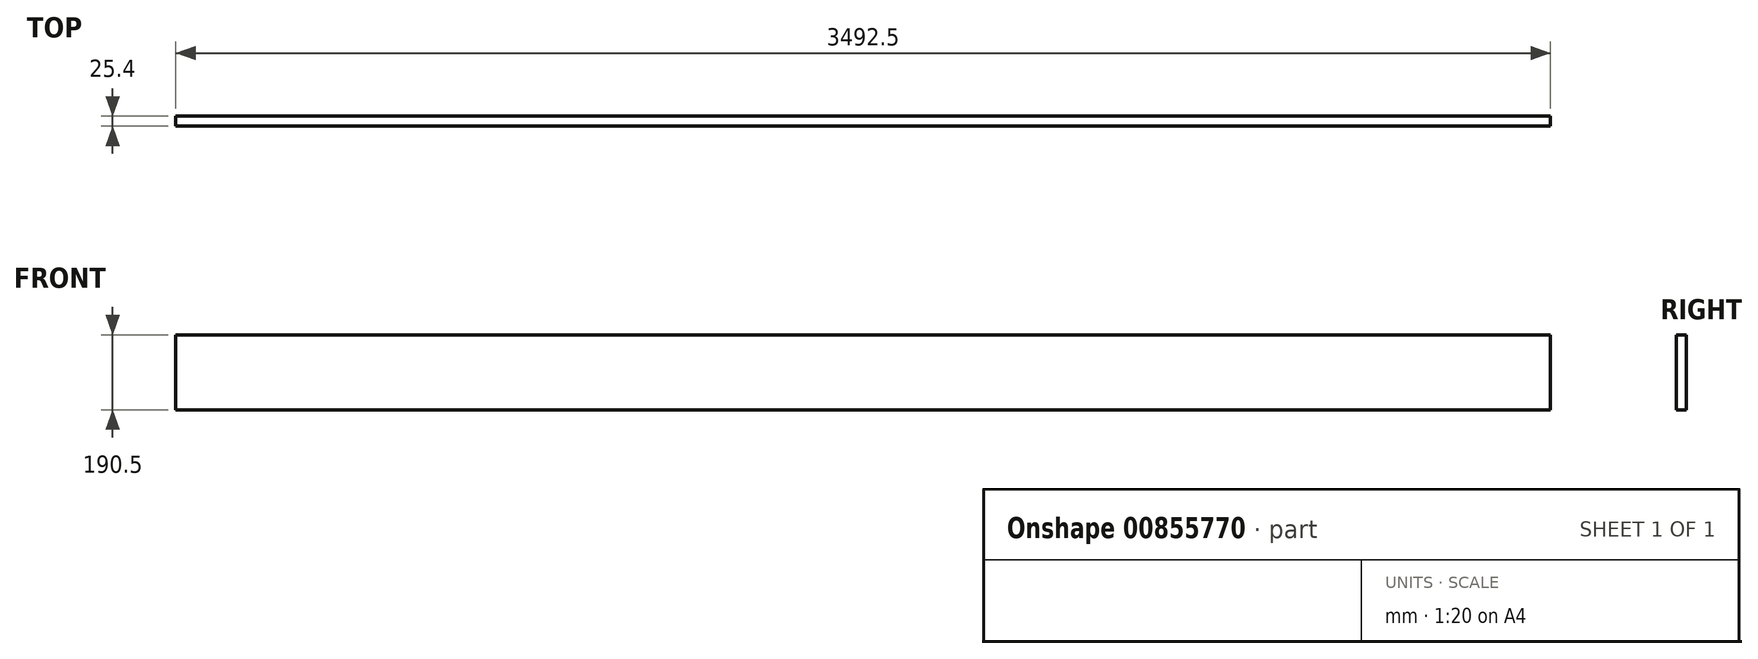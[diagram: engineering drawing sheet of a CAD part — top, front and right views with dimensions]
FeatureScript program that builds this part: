
annotation { "Feature Type Name" : "Feature", "Feature Type Description" : "" }
export const myFeature = defineFeature(function(context is Context, id is Id, definition is map)
    precondition{}
    {
        {
            var Q0;
            Q0=qCreatedBy(makeId("Right.planeOp"),FACE);
            var sketch = newSketch(context, id + "F0", { "sketchPlane" : qUnion([Q0])});
            skLineSegment(sketch, "E0.bottom", {"start": v(0, 0) * mm, "end": v(25.4, 0) * mm});
            skLineSegment(sketch, "E0.top", {"start": v(0, -190.5) * mm, "end": v(25.4, -190.5) * mm});
            skLineSegment(sketch, "E0.left", {"start": v(0, 0) * mm, "end": v(0, -190.5) * mm});
            skLineSegment(sketch, "E0.right", {"start": v(25.4, 0) * mm, "end": v(25.4, -190.5) * mm});
            skSolve(sketch);
        }
        {
            var Q0;
            Q0=makeQuery(id+"F0.imprint","IMPRINT",FACE,{"disambiguationData":[TD([[makeQuery(id+"F0.imprint","IMPRINT",EDGE,{"derivedFrom":sQuery(id+"F0.wireOp",EDGE,"E0.bottom")}),-1.0]])]});
            extrude(context, id + "F1", {"entities" : qUnion([Q0]), "depth" : 3492.5 * mm, "offsetDistance" : 25.4 * mm});
        }
    });
